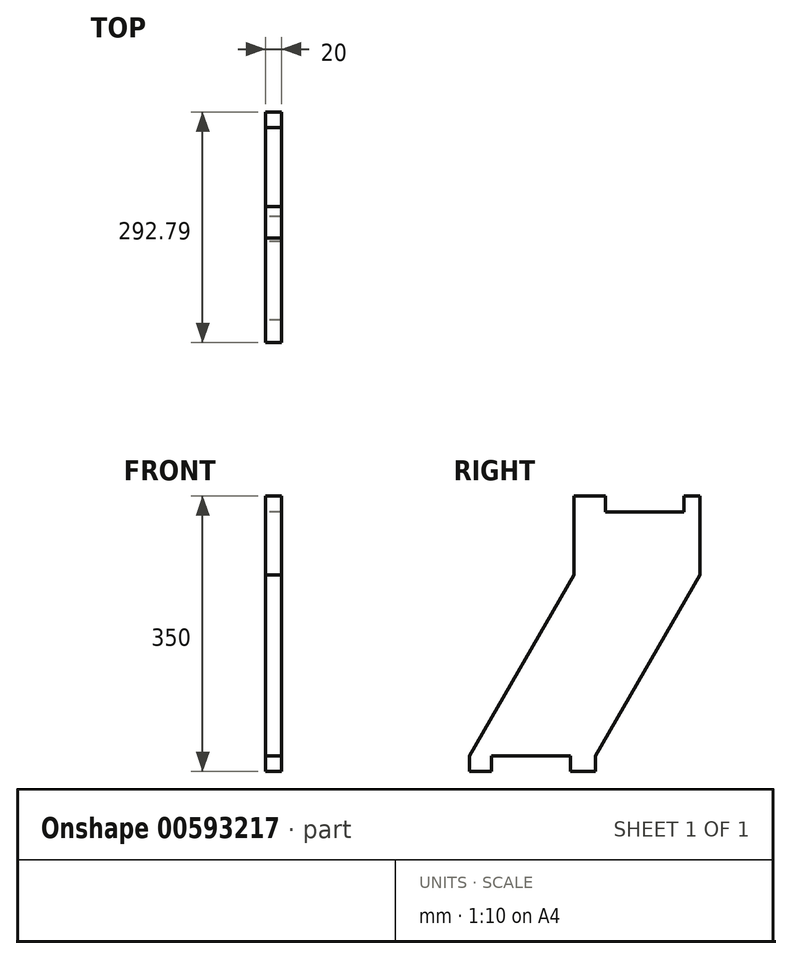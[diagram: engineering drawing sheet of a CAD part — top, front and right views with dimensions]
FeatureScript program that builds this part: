
annotation { "Feature Type Name" : "Feature", "Feature Type Description" : "" }
export const myFeature = defineFeature(function(context is Context, id is Id, definition is map)
    precondition{}
    {
        {
            var Q0;
            Q0=qCreatedBy(makeId("Right.planeOp"),FACE);
            var sketch = newSketch(context, id + "F0", { "sketchPlane" : qUnion([Q0])});
            skLineSegment(sketch, "E0", {"start": v(-144.34, 0) * mm, "end": v(15.66, 0) * mm});
            skLineSegment(sketch, "E1", {"start": v(-144.34, 0) * mm, "end": v(0, 250) * mm});
            skLineSegment(sketch, "E2", {"start": v(15.66, 0) * mm, "end": v(160, 250) * mm});
            skLineSegment(sketch, "E3", {"start": v(160, 250) * mm, "end": v(0, 250) * mm});
            skLineSegment(sketch, "E4.bottom", {"start": v(-4.34, 0) * mm, "end": v(-104.34, 0) * mm});
            skLineSegment(sketch, "E4.top", {"start": v(-4.34, 20) * mm, "end": v(-104.34, 20) * mm});
            skLineSegment(sketch, "E4.left", {"start": v(-4.34, 0) * mm, "end": v(-4.34, 20) * mm});
            skLineSegment(sketch, "E4.right", {"start": v(-104.34, 0) * mm, "end": v(-104.34, 20) * mm});
            skLineSegment(sketch, "E5", {"start": v(-132.8, 20) * mm, "end": v(-132.8, 0) * mm});
            skLineSegment(sketch, "E6", {"start": v(27.2, 20) * mm, "end": v(27.2, 0) * mm});
            skLineSegment(sketch, "E7", {"start": v(27.2, 0) * mm, "end": v(15.66, 0) * mm});
            skLineSegment(sketch, "E8.top", {"start": v(160, 350) * mm, "end": v(0, 350) * mm});
            skLineSegment(sketch, "E8.left", {"start": v(160, 250) * mm, "end": v(160, 350) * mm});
            skLineSegment(sketch, "E8.right", {"start": v(0, 250) * mm, "end": v(0, 350) * mm});
            skLineSegment(sketch, "E9.bottom", {"start": v(140, 350) * mm, "end": v(40, 350) * mm});
            skLineSegment(sketch, "E9.top", {"start": v(140, 330) * mm, "end": v(40, 330) * mm});
            skLineSegment(sketch, "E9.left", {"start": v(140, 350) * mm, "end": v(140, 330) * mm});
            skLineSegment(sketch, "E9.right", {"start": v(40, 350) * mm, "end": v(40, 330) * mm});
            skSolve(sketch);
        }
        {
            var Q0;
            Q0=makeQuery(id+"F0.imprint","IMPRINT",FACE,{"disambiguationData":[TD([[makeQuery(id+"F0.imprint","IMPRINT",EDGE,{"derivedFrom":sQuery(id+"F0.wireOp",EDGE,"E0")}),1.0]])]});
            var Q1;
            {var subQ2=sQuery(id+"F0.wireOp",EDGE,"E6");Q1=makeQuery(id+"F0.imprint","IMPRINT",FACE,{"disambiguationData":[TD([[makeQuery(id+"F0.imprint","IMPRINT",EDGE,{"derivedFrom":subQ2}),-1.0]])]});}
            var Q2;
            Q2=makeQuery(id+"F0.imprint","IMPRINT",FACE,{"disambiguationData":[TD([[makeQuery(id+"F0.imprint","IMPRINT",EDGE,{"derivedFrom":sQuery(id+"F0.wireOp",EDGE,"E3")}),-1.0]])]});
            extrude(context, id + "F1", {"entities" : qUnion([Q0, Q1, Q2]), "depth" : 20 * mm, "offsetDistance" : 25 * mm});
        }
    });
